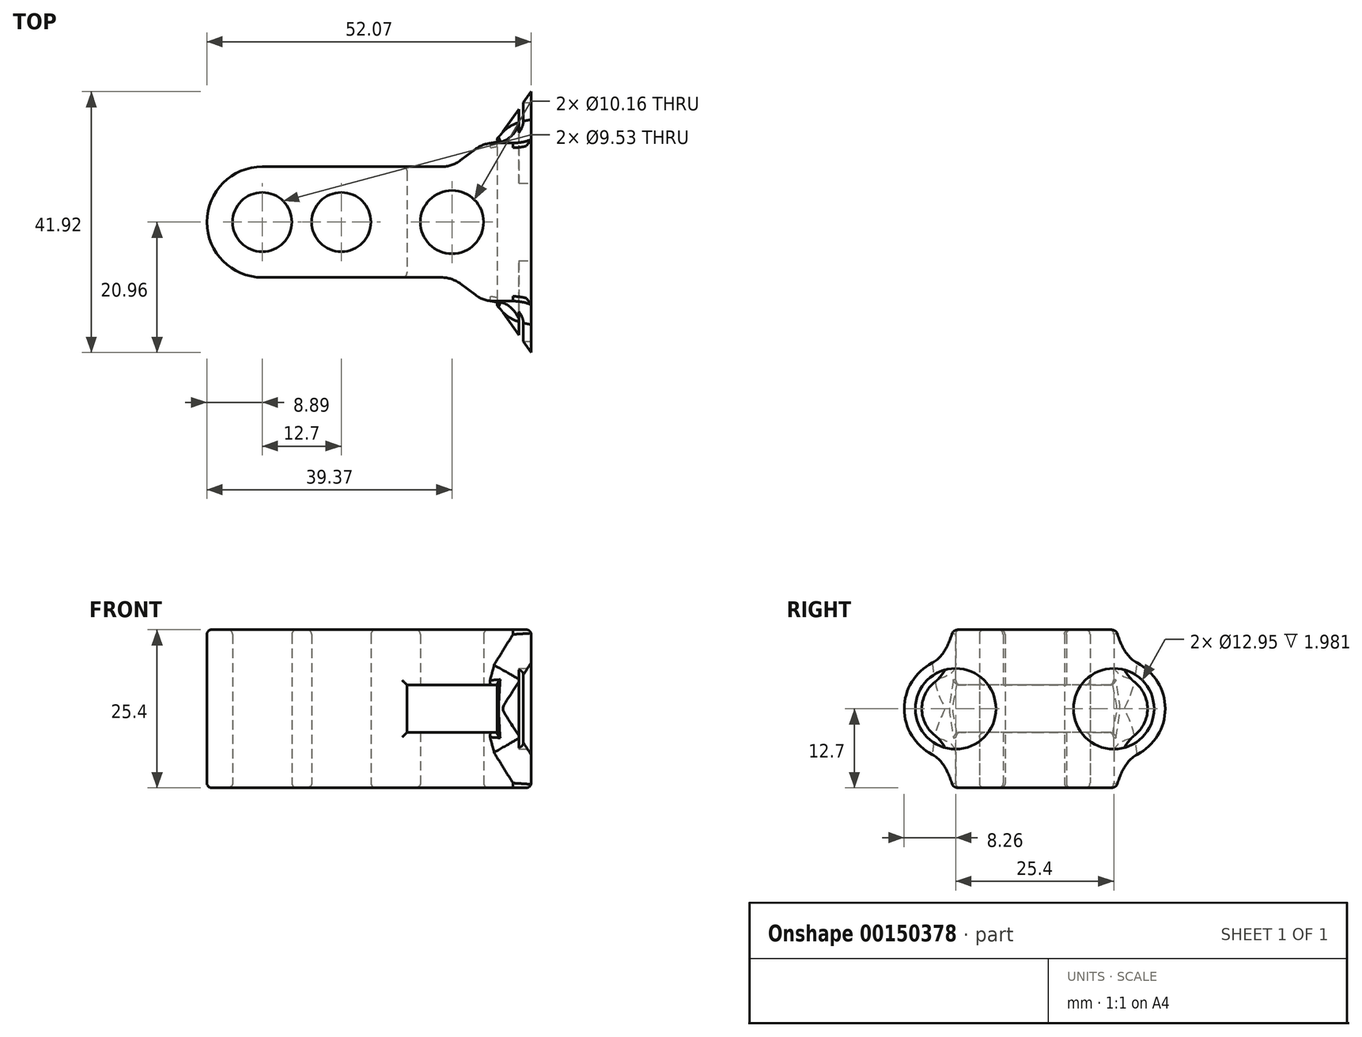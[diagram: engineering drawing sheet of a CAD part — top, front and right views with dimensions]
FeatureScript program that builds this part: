
annotation { "Feature Type Name" : "Feature", "Feature Type Description" : "" }
export const myFeature = defineFeature(function(context is Context, id is Id, definition is map)
    precondition{}
    {
        {
            var Q0;
            Q0=qCreatedBy(makeId("Top.planeOp"),FACE);
            var sketch = newSketch(context, id + "F0", { "sketchPlane" : qUnion([Q0])});
            skCircle(sketch, "E0", {"center": v(-12.7, 0) * mm, "radius": 4.76 * mm});
            skCircle(sketch, "E1", {"center": v(0, 0) * mm, "radius": 4.76 * mm});
            skCircle(sketch, "E2", {"center": v(17.78, 0) * mm, "radius": 5.08 * mm});
            skArc(sketch, "E3", {"start": v(-12.7, 8.9) * mm, "mid": v(-21.59, 0) * mm, "end": v(-12.7, -8.9) * mm});
            skLineSegment(sketch, "E4", {"start": v(-12.7, 8.9) * mm, "end": v(17.78, 8.9) * mm});
            skLineSegment(sketch, "E5", {"start": v(-12.7, 0) * mm, "end": v(-12.7, 8.9) * mm, "construction": true});
            skLineSegment(sketch, "E6", {"start": v(17.78, 0) * mm, "end": v(17.78, 8.9) * mm, "construction": true});
            skLineSegment(sketch, "E7", {"start": v(-12.7, -8.9) * mm, "end": v(17.78, -8.9) * mm});
            skLineSegment(sketch, "E8", {"start": v(30.48, 12.7) * mm, "end": v(30.48, -12.7) * mm});
            skLineSegment(sketch, "E9", {"start": v(30.48, -12.7) * mm, "end": v(22.86, -12.7) * mm});
            skLineSegment(sketch, "E10", {"start": v(22.86, -12.7) * mm, "end": v(17.78, -8.9) * mm});
            skLineSegment(sketch, "E11", {"start": v(30.48, 12.7) * mm, "end": v(22.86, 12.7) * mm});
            skLineSegment(sketch, "E12", {"start": v(22.86, 12.7) * mm, "end": v(17.78, 8.9) * mm});
            skLineSegment(sketch, "E13", {"start": v(17.78, 0) * mm, "end": v(30.48, 0) * mm, "construction": true});
            skLineSegment(sketch, "E14", {"start": v(17.78, 0) * mm, "end": v(17.78, -8.9) * mm, "construction": true});
            skSolve(sketch);
        }
        {
            var Q0;
            Q0 = qSketchRegion(id + "F0", true);
            extrude(context, id + "F1", {"entities" : qUnion([Q0]), "depth" : 25.4 * mm});
        }
        {
            var Q0;
            Q0=qCreatedBy(makeId("Front.planeOp"),FACE);
            var sketch = newSketch(context, id + "F2", { "sketchPlane" : qUnion([Q0])});
            skLineSegment(sketch, "E15.bottom", {"start": v(10.54, 8.9) * mm, "end": v(25.02, 8.9) * mm});
            skLineSegment(sketch, "E15.top", {"start": v(10.54, 16.51) * mm, "end": v(25.02, 16.51) * mm});
            skLineSegment(sketch, "E15.left", {"start": v(10.54, 8.9) * mm, "end": v(10.54, 16.51) * mm});
            skLineSegment(sketch, "E15.right", {"start": v(25.02, 8.9) * mm, "end": v(25.02, 16.51) * mm});
            skLineSegment(sketch, "E16", {"start": v(10.54, 12.7) * mm, "end": v(0, 12.7) * mm, "construction": true});
            skLineSegment(sketch, "E17", {"start": v(17.78, 16.51) * mm, "end": v(17.78, 25.4) * mm, "construction": true});
            skSolve(sketch);
        }
        {
            var Q0;
            Q0 = qSketchRegion(id + "F2", true);
            extrude(context, id + "F3", {"entities" : qUnion([Q0]), "operationType" : NewBodyOperationType.REMOVE, "endBound" : BoundingType.SYMMETRIC, "oppositeDirection" : true, "depth" : 25.4 * mm});
        }
        {
            var Q0;
            Q0=makeQuery(id+"F1.opExtrude","SWEPT_FACE",FACE,{"disambiguationData":[OSD([sQuery(id+"F0.wireOp",EDGE,"E8")])]});
            var sketch = newSketch(context, id + "F4", { "sketchPlane" : qUnion([Q0])});
            skCircle(sketch, "E18", {"center": v(-12.7, 12.7) * mm, "radius": 8.26 * mm});
            skCircle(sketch, "E19", {"center": v(12.7, 12.7) * mm, "radius": 8.26 * mm});
            skLineSegment(sketch, "E20", {"start": v(-12.7, 12.7) * mm, "end": v(0, 0) * mm, "construction": true});
            skLineSegment(sketch, "E21", {"start": v(0, 0) * mm, "end": v(12.7, 12.7) * mm, "construction": true});
            skLineSegment(sketch, "E22", {"start": v(-12.7, 12.7) * mm, "end": v(12.7, 12.7) * mm, "construction": true});
            skSolve(sketch);
        }
        {
            var Q0;
            Q0 = qSketchRegion(id + "F4", true);
            extrude(context, id + "F5", {"entities" : qUnion([Q0]), "operationType" : NewBodyOperationType.ADD, "oppositeDirection" : true, "depth" : 5.46 * mm, "hasDraft" : true, "draftAngle" : 55 * degree, "draftPullDirection" : true});
        }
        {
            var Q0;
            {var subQ0=sQuery(id+"F0.wireOp",EDGE,"E12");var subQ1=sQuery(id+"F0.wireOp",EDGE,"E11");Q0=makeQuery(id+"F3.boolean.opBoolean","SPLIT",EDGE,{"disambiguationData":[TD([makeQuery(id+"F3.opExtrude","SWEPT_FACE",FACE,{"disambiguationData":[OSD([sQuery(id+"F2.wireOp",EDGE,"E15.bottom")])]})])],"derivedFrom":makeQuery(id+"F1.opExtrude","SWEPT_EDGE",EDGE,{"disambiguationData":[OSD([subQ1,subQ0])]})});}
            var Q1;
            {var subQ0=sQuery(id+"F0.wireOp",EDGE,"E12");var subQ1=sQuery(id+"F0.wireOp",EDGE,"E4");Q1=makeQuery(id+"F3.boolean.opBoolean","SPLIT",EDGE,{"disambiguationData":[TD([makeQuery(id+"F3.opExtrude","SWEPT_FACE",FACE,{"disambiguationData":[OSD([sQuery(id+"F2.wireOp",EDGE,"E15.bottom")])]})])],"derivedFrom":makeQuery(id+"F1.opExtrude","SWEPT_EDGE",EDGE,{"disambiguationData":[OSD([subQ1,subQ0])]})});}
            var Q2;
            {var subQ0=sQuery(id+"F0.wireOp",EDGE,"E12");var subQ1=sQuery(id+"F0.wireOp",EDGE,"E4");Q2=makeQuery(id+"F3.boolean.opBoolean","SPLIT",EDGE,{"disambiguationData":[TD([makeQuery(id+"F3.opExtrude","SWEPT_FACE",FACE,{"disambiguationData":[OSD([sQuery(id+"F2.wireOp",EDGE,"E15.top")])]})])],"derivedFrom":makeQuery(id+"F1.opExtrude","SWEPT_EDGE",EDGE,{"disambiguationData":[OSD([subQ1,subQ0])]})});}
            var Q3;
            {var subQ0=sQuery(id+"F0.wireOp",EDGE,"E12");var subQ1=sQuery(id+"F0.wireOp",EDGE,"E11");Q3=makeQuery(id+"F3.boolean.opBoolean","SPLIT",EDGE,{"disambiguationData":[TD([makeQuery(id+"F3.opExtrude","SWEPT_FACE",FACE,{"disambiguationData":[OSD([sQuery(id+"F2.wireOp",EDGE,"E15.top")])]})])],"derivedFrom":makeQuery(id+"F1.opExtrude","SWEPT_EDGE",EDGE,{"disambiguationData":[OSD([subQ1,subQ0])]})});}
            var Q4;
            {var subQ0=sQuery(id+"F0.wireOp",EDGE,"E10");var subQ1=sQuery(id+"F0.wireOp",EDGE,"E7");Q4=makeQuery(id+"F3.boolean.opBoolean","SPLIT",EDGE,{"disambiguationData":[TD([makeQuery(id+"F3.opExtrude","SWEPT_FACE",FACE,{"disambiguationData":[OSD([sQuery(id+"F2.wireOp",EDGE,"E15.top")])]})])],"derivedFrom":makeQuery(id+"F1.opExtrude","SWEPT_EDGE",EDGE,{"disambiguationData":[OSD([subQ1,subQ0])]})});}
            var Q5;
            {var subQ0=sQuery(id+"F0.wireOp",EDGE,"E10");var subQ1=sQuery(id+"F0.wireOp",EDGE,"E9");Q5=makeQuery(id+"F3.boolean.opBoolean","SPLIT",EDGE,{"disambiguationData":[TD([makeQuery(id+"F3.opExtrude","SWEPT_FACE",FACE,{"disambiguationData":[OSD([sQuery(id+"F2.wireOp",EDGE,"E15.top")])]})])],"derivedFrom":makeQuery(id+"F1.opExtrude","SWEPT_EDGE",EDGE,{"disambiguationData":[OSD([subQ1,subQ0])]})});}
            var Q6;
            {var subQ0=sQuery(id+"F0.wireOp",EDGE,"E10");var subQ1=sQuery(id+"F0.wireOp",EDGE,"E7");Q6=makeQuery(id+"F3.boolean.opBoolean","SPLIT",EDGE,{"disambiguationData":[TD([makeQuery(id+"F3.opExtrude","SWEPT_FACE",FACE,{"disambiguationData":[OSD([sQuery(id+"F2.wireOp",EDGE,"E15.bottom")])]})])],"derivedFrom":makeQuery(id+"F1.opExtrude","SWEPT_EDGE",EDGE,{"disambiguationData":[OSD([subQ1,subQ0])]})});}
            var Q7;
            {var subQ0=sQuery(id+"F0.wireOp",EDGE,"E10");var subQ1=sQuery(id+"F0.wireOp",EDGE,"E9");Q7=makeQuery(id+"F3.boolean.opBoolean","SPLIT",EDGE,{"disambiguationData":[TD([makeQuery(id+"F3.opExtrude","SWEPT_FACE",FACE,{"disambiguationData":[OSD([sQuery(id+"F2.wireOp",EDGE,"E15.bottom")])]})])],"derivedFrom":makeQuery(id+"F1.opExtrude","SWEPT_EDGE",EDGE,{"disambiguationData":[OSD([subQ1,subQ0])]})});}
            fillet(context, id + "F6", {"entities" : qUnion([Q0, Q1, Q2, Q3, Q4, Q5, Q6, Q7]), "radius" : 5.08 * mm, "tangentPropagation" : true, "allowEdgeOverflow" : false});
        }
        {
            var Q0;
            Q0=makeQuery(id+"F5.boolean.opBoolean","INTERSECT",EDGE,{"disambiguationData":[OD(0.0)],"derivedFrom":[makeQuery(id+"F1.opExtrude","SWEPT_FACE",FACE,{"disambiguationData":[OSD([sQuery(id+"F0.wireOp",EDGE,"E9")])]}),makeQuery(id+"F5.opExtrude","SWEPT_FACE",FACE,{"disambiguationData":[OSD([sQuery(id+"F4.wireOp",EDGE,"E18")])]})]});
            var Q1;
            Q1=makeQuery(id+"F5.boolean.opBoolean","INTERSECT",EDGE,{"disambiguationData":[OD(1.0)],"derivedFrom":[makeQuery(id+"F1.opExtrude","SWEPT_FACE",FACE,{"disambiguationData":[OSD([sQuery(id+"F0.wireOp",EDGE,"E9")])]}),makeQuery(id+"F5.opExtrude","SWEPT_FACE",FACE,{"disambiguationData":[OSD([sQuery(id+"F4.wireOp",EDGE,"E18")])]})]});
            var Q2;
            Q2=makeQuery(id+"F5.boolean.opBoolean","INTERSECT",EDGE,{"disambiguationData":[OD(1.0)],"derivedFrom":[makeQuery(id+"F1.opExtrude","SWEPT_FACE",FACE,{"disambiguationData":[OSD([sQuery(id+"F0.wireOp",EDGE,"E11")])]}),makeQuery(id+"F5.opExtrude","SWEPT_FACE",FACE,{"disambiguationData":[OSD([sQuery(id+"F4.wireOp",EDGE,"E19")])]})]});
            var Q3;
            Q3=makeQuery(id+"F5.boolean.opBoolean","INTERSECT",EDGE,{"disambiguationData":[OD(0.0)],"derivedFrom":[makeQuery(id+"F1.opExtrude","SWEPT_FACE",FACE,{"disambiguationData":[OSD([sQuery(id+"F0.wireOp",EDGE,"E11")])]}),makeQuery(id+"F5.opExtrude","SWEPT_FACE",FACE,{"disambiguationData":[OSD([sQuery(id+"F4.wireOp",EDGE,"E19")])]})]});
            fillet(context, id + "F7", {"entities" : qUnion([Q0, Q1, Q2, Q3]), "radius" : 5.08 * mm, "tangentPropagation" : true, "allowEdgeOverflow" : false});
        }
        {
            var Q0;
            {var subQ0=sQuery(id+"F4.wireOp",EDGE,"E18");Q0=makeQuery(id+"F7.opFillet","BLEND_EDGE",EDGE,{"disambiguationData":[OD(1.0)],"blendedFrom":[makeQuery(id+"F5.boolean.opBoolean","INTERSECT",EDGE,{"disambiguationData":[OD(1.0)],"derivedFrom":[makeQuery(id+"F1.opExtrude","SWEPT_FACE",FACE,{"disambiguationData":[OSD([sQuery(id+"F0.wireOp",EDGE,"E9")])]}),makeQuery(id+"F5.opExtrude","SWEPT_FACE",FACE,{"disambiguationData":[OSD([subQ0])]})]}),makeQuery(id+"F5.boolean.opBoolean","MERGE",FACE,{"derivedFrom":[makeQuery(id+"F3.boolean.opBoolean","COPY",FACE,{"derivedFrom":makeQuery(id+"F3.opExtrude","SWEPT_FACE",FACE,{"disambiguationData":[OSD([sQuery(id+"F2.wireOp",EDGE,"E15.right")])]})}),makeQuery(id+"F5.opExtrude","CAP_FACE",FACE,{"disambiguationData":[OSD([subQ0])],"isStart":false}),makeQuery(id+"F5.opExtrude","CAP_FACE",FACE,{"disambiguationData":[OSD([sQuery(id+"F4.wireOp",EDGE,"E19")])],"isStart":false})]})],"blendedInto":[makeQuery(id+"F5.boolean.opBoolean","MERGE",FACE,{"derivedFrom":[makeQuery(id+"F3.boolean.opBoolean","COPY",FACE,{"derivedFrom":makeQuery(id+"F3.opExtrude","SWEPT_FACE",FACE,{"disambiguationData":[OSD([sQuery(id+"F2.wireOp",EDGE,"E15.right")])]})}),makeQuery(id+"F5.opExtrude","CAP_FACE",FACE,{"disambiguationData":[OSD([subQ0])],"isStart":false}),makeQuery(id+"F5.opExtrude","CAP_FACE",FACE,{"disambiguationData":[OSD([sQuery(id+"F4.wireOp",EDGE,"E19")])],"isStart":false})]})]});}
            var Q1;
            Q1=makeQuery(id+"F5.opExtrude","CAP_EDGE",EDGE,{"disambiguationData":[OSD([sQuery(id+"F4.wireOp",EDGE,"E18")])],"isStart":false});
            var Q2;
            {var subQ0=sQuery(id+"F4.wireOp",EDGE,"E18");Q2=makeQuery(id+"F7.opFillet","BLEND_EDGE",EDGE,{"disambiguationData":[OD(1.0)],"blendedFrom":[makeQuery(id+"F5.boolean.opBoolean","INTERSECT",EDGE,{"disambiguationData":[OD(0.0)],"derivedFrom":[makeQuery(id+"F1.opExtrude","SWEPT_FACE",FACE,{"disambiguationData":[OSD([sQuery(id+"F0.wireOp",EDGE,"E9")])]}),makeQuery(id+"F5.opExtrude","SWEPT_FACE",FACE,{"disambiguationData":[OSD([subQ0])]})]}),makeQuery(id+"F5.boolean.opBoolean","MERGE",FACE,{"derivedFrom":[makeQuery(id+"F3.boolean.opBoolean","COPY",FACE,{"derivedFrom":makeQuery(id+"F3.opExtrude","SWEPT_FACE",FACE,{"disambiguationData":[OSD([sQuery(id+"F2.wireOp",EDGE,"E15.right")])]})}),makeQuery(id+"F5.opExtrude","CAP_FACE",FACE,{"disambiguationData":[OSD([subQ0])],"isStart":false}),makeQuery(id+"F5.opExtrude","CAP_FACE",FACE,{"disambiguationData":[OSD([sQuery(id+"F4.wireOp",EDGE,"E19")])],"isStart":false})]})],"blendedInto":[makeQuery(id+"F5.boolean.opBoolean","MERGE",FACE,{"derivedFrom":[makeQuery(id+"F3.boolean.opBoolean","COPY",FACE,{"derivedFrom":makeQuery(id+"F3.opExtrude","SWEPT_FACE",FACE,{"disambiguationData":[OSD([sQuery(id+"F2.wireOp",EDGE,"E15.right")])]})}),makeQuery(id+"F5.opExtrude","CAP_FACE",FACE,{"disambiguationData":[OSD([subQ0])],"isStart":false}),makeQuery(id+"F5.opExtrude","CAP_FACE",FACE,{"disambiguationData":[OSD([sQuery(id+"F4.wireOp",EDGE,"E19")])],"isStart":false})]})]});}
            var Q3;
            Q3=makeQuery(id+"F3.boolean.opBoolean","INTERSECT",EDGE,{"derivedFrom":[makeQuery(id+"F1.opExtrude","SWEPT_FACE",FACE,{"disambiguationData":[OSD([sQuery(id+"F0.wireOp",EDGE,"E10")])]}),makeQuery(id+"F3.opExtrude","SWEPT_FACE",FACE,{"disambiguationData":[OSD([sQuery(id+"F2.wireOp",EDGE,"E15.top")])]})]});
            var Q4;
            Q4=makeQuery(id+"F3.boolean.opBoolean","INTERSECT",EDGE,{"derivedFrom":[makeQuery(id+"F1.opExtrude","SWEPT_FACE",FACE,{"disambiguationData":[OSD([sQuery(id+"F0.wireOp",EDGE,"E7")])]}),makeQuery(id+"F3.opExtrude","SWEPT_FACE",FACE,{"disambiguationData":[OSD([sQuery(id+"F2.wireOp",EDGE,"E15.top")])]})]});
            var Q5;
            Q5=makeQuery(id+"F3.boolean.opBoolean","INTERSECT",EDGE,{"derivedFrom":[makeQuery(id+"F1.opExtrude","SWEPT_FACE",FACE,{"disambiguationData":[OSD([sQuery(id+"F0.wireOp",EDGE,"E7")])]}),makeQuery(id+"F3.opExtrude","SWEPT_FACE",FACE,{"disambiguationData":[OSD([sQuery(id+"F2.wireOp",EDGE,"E15.left")])]})]});
            var Q6;
            Q6=makeQuery(id+"F3.boolean.opBoolean","INTERSECT",EDGE,{"derivedFrom":[makeQuery(id+"F1.opExtrude","SWEPT_FACE",FACE,{"disambiguationData":[OSD([sQuery(id+"F0.wireOp",EDGE,"E7")])]}),makeQuery(id+"F3.opExtrude","SWEPT_FACE",FACE,{"disambiguationData":[OSD([sQuery(id+"F2.wireOp",EDGE,"E15.bottom")])]})]});
            var Q7;
            Q7=makeQuery(id+"F3.boolean.opBoolean","INTERSECT",EDGE,{"derivedFrom":[makeQuery(id+"F1.opExtrude","SWEPT_FACE",FACE,{"disambiguationData":[OSD([sQuery(id+"F0.wireOp",EDGE,"E10")])]}),makeQuery(id+"F3.opExtrude","SWEPT_FACE",FACE,{"disambiguationData":[OSD([sQuery(id+"F2.wireOp",EDGE,"E15.bottom")])]})]});
            var Q8;
            Q8=makeQuery(id+"F7.opFillet","BLEND_EDGE",EDGE,{"disambiguationData":[OD(0.0)],"blendedFrom":[makeQuery(id+"F5.boolean.opBoolean","INTERSECT",EDGE,{"disambiguationData":[OD(0.0)],"derivedFrom":[makeQuery(id+"F1.opExtrude","SWEPT_FACE",FACE,{"disambiguationData":[OSD([sQuery(id+"F0.wireOp",EDGE,"E9")])]}),makeQuery(id+"F5.opExtrude","SWEPT_FACE",FACE,{"disambiguationData":[OSD([sQuery(id+"F4.wireOp",EDGE,"E18")])]})]}),makeQuery(id+"F3.boolean.opBoolean","COPY",FACE,{"derivedFrom":makeQuery(id+"F3.opExtrude","SWEPT_FACE",FACE,{"disambiguationData":[OSD([sQuery(id+"F2.wireOp",EDGE,"E15.bottom")])]})})],"blendedInto":[makeQuery(id+"F3.boolean.opBoolean","COPY",FACE,{"derivedFrom":makeQuery(id+"F3.opExtrude","SWEPT_FACE",FACE,{"disambiguationData":[OSD([sQuery(id+"F2.wireOp",EDGE,"E15.bottom")])]})})]});
            var Q9;
            {var subQ0=sQuery(id+"F4.wireOp",EDGE,"E19");Q9=makeQuery(id+"F7.opFillet","BLEND_EDGE",EDGE,{"disambiguationData":[OD(1.0)],"blendedFrom":[makeQuery(id+"F5.boolean.opBoolean","INTERSECT",EDGE,{"disambiguationData":[OD(1.0)],"derivedFrom":[makeQuery(id+"F1.opExtrude","SWEPT_FACE",FACE,{"disambiguationData":[OSD([sQuery(id+"F0.wireOp",EDGE,"E11")])]}),makeQuery(id+"F5.opExtrude","SWEPT_FACE",FACE,{"disambiguationData":[OSD([subQ0])]})]}),makeQuery(id+"F5.boolean.opBoolean","MERGE",FACE,{"derivedFrom":[makeQuery(id+"F3.boolean.opBoolean","COPY",FACE,{"derivedFrom":makeQuery(id+"F3.opExtrude","SWEPT_FACE",FACE,{"disambiguationData":[OSD([sQuery(id+"F2.wireOp",EDGE,"E15.right")])]})}),makeQuery(id+"F5.opExtrude","CAP_FACE",FACE,{"disambiguationData":[OSD([sQuery(id+"F4.wireOp",EDGE,"E18")])],"isStart":false}),makeQuery(id+"F5.opExtrude","CAP_FACE",FACE,{"disambiguationData":[OSD([subQ0])],"isStart":false})]})],"blendedInto":[makeQuery(id+"F5.boolean.opBoolean","MERGE",FACE,{"derivedFrom":[makeQuery(id+"F3.boolean.opBoolean","COPY",FACE,{"derivedFrom":makeQuery(id+"F3.opExtrude","SWEPT_FACE",FACE,{"disambiguationData":[OSD([sQuery(id+"F2.wireOp",EDGE,"E15.right")])]})}),makeQuery(id+"F5.opExtrude","CAP_FACE",FACE,{"disambiguationData":[OSD([sQuery(id+"F4.wireOp",EDGE,"E18")])],"isStart":false}),makeQuery(id+"F5.opExtrude","CAP_FACE",FACE,{"disambiguationData":[OSD([subQ0])],"isStart":false})]})]});}
            var Q10;
            Q10=makeQuery(id+"F7.opFillet","BLEND_EDGE",EDGE,{"disambiguationData":[OD(0.0)],"blendedFrom":[makeQuery(id+"F5.boolean.opBoolean","INTERSECT",EDGE,{"disambiguationData":[OD(1.0)],"derivedFrom":[makeQuery(id+"F1.opExtrude","SWEPT_FACE",FACE,{"disambiguationData":[OSD([sQuery(id+"F0.wireOp",EDGE,"E11")])]}),makeQuery(id+"F5.opExtrude","SWEPT_FACE",FACE,{"disambiguationData":[OSD([sQuery(id+"F4.wireOp",EDGE,"E19")])]})]}),makeQuery(id+"F3.boolean.opBoolean","COPY",FACE,{"derivedFrom":makeQuery(id+"F3.opExtrude","SWEPT_FACE",FACE,{"disambiguationData":[OSD([sQuery(id+"F2.wireOp",EDGE,"E15.top")])]})})],"blendedInto":[makeQuery(id+"F3.boolean.opBoolean","COPY",FACE,{"derivedFrom":makeQuery(id+"F3.opExtrude","SWEPT_FACE",FACE,{"disambiguationData":[OSD([sQuery(id+"F2.wireOp",EDGE,"E15.top")])]})})]});
            var Q11;
            Q11=makeQuery(id+"F3.boolean.opBoolean","INTERSECT",EDGE,{"derivedFrom":[makeQuery(id+"F1.opExtrude","SWEPT_FACE",FACE,{"disambiguationData":[OSD([sQuery(id+"F0.wireOp",EDGE,"E12")])]}),makeQuery(id+"F3.opExtrude","SWEPT_FACE",FACE,{"disambiguationData":[OSD([sQuery(id+"F2.wireOp",EDGE,"E15.top")])]})]});
            var Q12;
            Q12=makeQuery(id+"F3.boolean.opBoolean","INTERSECT",EDGE,{"derivedFrom":[makeQuery(id+"F1.opExtrude","SWEPT_FACE",FACE,{"disambiguationData":[OSD([sQuery(id+"F0.wireOp",EDGE,"E4")])]}),makeQuery(id+"F3.opExtrude","SWEPT_FACE",FACE,{"disambiguationData":[OSD([sQuery(id+"F2.wireOp",EDGE,"E15.top")])]})]});
            var Q13;
            Q13=makeQuery(id+"F3.boolean.opBoolean","INTERSECT",EDGE,{"derivedFrom":[makeQuery(id+"F1.opExtrude","SWEPT_FACE",FACE,{"disambiguationData":[OSD([sQuery(id+"F0.wireOp",EDGE,"E4")])]}),makeQuery(id+"F3.opExtrude","SWEPT_FACE",FACE,{"disambiguationData":[OSD([sQuery(id+"F2.wireOp",EDGE,"E15.left")])]})]});
            var Q14;
            Q14=makeQuery(id+"F3.boolean.opBoolean","INTERSECT",EDGE,{"derivedFrom":[makeQuery(id+"F1.opExtrude","SWEPT_FACE",FACE,{"disambiguationData":[OSD([sQuery(id+"F0.wireOp",EDGE,"E4")])]}),makeQuery(id+"F3.opExtrude","SWEPT_FACE",FACE,{"disambiguationData":[OSD([sQuery(id+"F2.wireOp",EDGE,"E15.bottom")])]})]});
            var Q15;
            Q15=makeQuery(id+"F3.boolean.opBoolean","INTERSECT",EDGE,{"derivedFrom":[makeQuery(id+"F1.opExtrude","SWEPT_FACE",FACE,{"disambiguationData":[OSD([sQuery(id+"F0.wireOp",EDGE,"E12")])]}),makeQuery(id+"F3.opExtrude","SWEPT_FACE",FACE,{"disambiguationData":[OSD([sQuery(id+"F2.wireOp",EDGE,"E15.bottom")])]})]});
            var Q16;
            Q16=makeQuery(id+"F7.opFillet","BLEND_EDGE",EDGE,{"disambiguationData":[OD(0.0)],"blendedFrom":[makeQuery(id+"F5.boolean.opBoolean","INTERSECT",EDGE,{"disambiguationData":[OD(0.0)],"derivedFrom":[makeQuery(id+"F1.opExtrude","SWEPT_FACE",FACE,{"disambiguationData":[OSD([sQuery(id+"F0.wireOp",EDGE,"E11")])]}),makeQuery(id+"F5.opExtrude","SWEPT_FACE",FACE,{"disambiguationData":[OSD([sQuery(id+"F4.wireOp",EDGE,"E19")])]})]}),makeQuery(id+"F3.boolean.opBoolean","COPY",FACE,{"derivedFrom":makeQuery(id+"F3.opExtrude","SWEPT_FACE",FACE,{"disambiguationData":[OSD([sQuery(id+"F2.wireOp",EDGE,"E15.bottom")])]})})],"blendedInto":[makeQuery(id+"F3.boolean.opBoolean","COPY",FACE,{"derivedFrom":makeQuery(id+"F3.opExtrude","SWEPT_FACE",FACE,{"disambiguationData":[OSD([sQuery(id+"F2.wireOp",EDGE,"E15.bottom")])]})})]});
            fillet(context, id + "F8", {"entities" : qUnion([Q0, Q1, Q2, Q3, Q4, Q5, Q6, Q7, Q8, Q9, Q10, Q11, Q12, Q13, Q14, Q15, Q16]), "radius" : 0.76 * mm, "tangentPropagation" : true, "allowEdgeOverflow" : false});
        }
        {
            var Q0;
            Q0=makeQuery(id+"F5.boolean.opBoolean","MERGE",FACE,{"derivedFrom":[makeQuery(id+"F1.opExtrude","SWEPT_FACE",FACE,{"disambiguationData":[OSD([sQuery(id+"F0.wireOp",EDGE,"E8")])]}),makeQuery(id+"F5.opExtrude","CAP_FACE",FACE,{"disambiguationData":[OSD([sQuery(id+"F4.wireOp",EDGE,"E18")])],"isStart":true}),makeQuery(id+"F5.opExtrude","CAP_FACE",FACE,{"disambiguationData":[OSD([sQuery(id+"F4.wireOp",EDGE,"E19")])],"isStart":true})]});
            var sketch = newSketch(context, id + "F9", { "sketchPlane" : qUnion([Q0])});
            skCircle(sketch, "E23", {"center": v(-12.7, 12.7) * mm, "radius": 6.48 * mm});
            skCircle(sketch, "E24", {"center": v(12.7, 12.7) * mm, "radius": 6.48 * mm});
            skSolve(sketch);
        }
        {
            var Q0;
            Q0 = qSketchRegion(id + "F9", true);
            extrude(context, id + "F10", {"entities" : qUnion([Q0]), "operationType" : NewBodyOperationType.REMOVE, "oppositeDirection" : true, "depth" : 1.98 * mm});
        }
        {
            var Q0;
            Q0=makeQuery(id+"F1.opExtrude","CAP_FACE",FACE,{"disambiguationData":[OSD([sQuery(id+"F0.wireOp",EDGE,"E0"),sQuery(id+"F0.wireOp",EDGE,"E1"),sQuery(id+"F0.wireOp",EDGE,"E2"),sQuery(id+"F0.wireOp",EDGE,"E3"),sQuery(id+"F0.wireOp",EDGE,"E4"),sQuery(id+"F0.wireOp",EDGE,"E7"),sQuery(id+"F0.wireOp",EDGE,"E8"),sQuery(id+"F0.wireOp",EDGE,"E9"),sQuery(id+"F0.wireOp",EDGE,"E10"),sQuery(id+"F0.wireOp",EDGE,"E11"),sQuery(id+"F0.wireOp",EDGE,"E12")])],"isStart":false});
            var Q1;
            Q1=makeQuery(id+"F1.opExtrude","CAP_FACE",FACE,{"disambiguationData":[OSD([sQuery(id+"F0.wireOp",EDGE,"E0"),sQuery(id+"F0.wireOp",EDGE,"E1"),sQuery(id+"F0.wireOp",EDGE,"E2"),sQuery(id+"F0.wireOp",EDGE,"E3"),sQuery(id+"F0.wireOp",EDGE,"E4"),sQuery(id+"F0.wireOp",EDGE,"E7"),sQuery(id+"F0.wireOp",EDGE,"E8"),sQuery(id+"F0.wireOp",EDGE,"E9"),sQuery(id+"F0.wireOp",EDGE,"E10"),sQuery(id+"F0.wireOp",EDGE,"E11"),sQuery(id+"F0.wireOp",EDGE,"E12")])],"isStart":true});
            fillet(context, id + "F11", {"entities" : qUnion([Q0, Q1]), "radius" : 0.76 * mm, "tangentPropagation" : true, "allowEdgeOverflow" : false});
        }
    });
